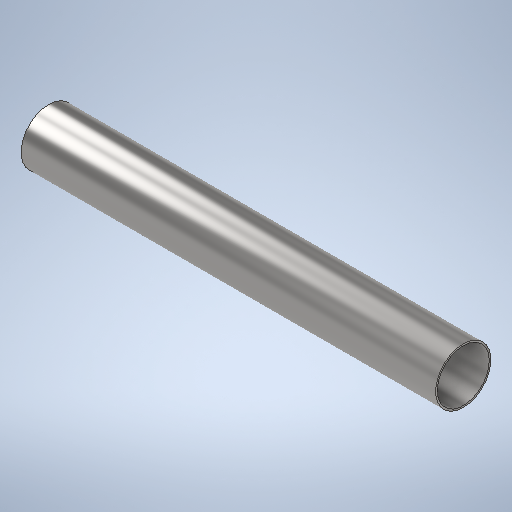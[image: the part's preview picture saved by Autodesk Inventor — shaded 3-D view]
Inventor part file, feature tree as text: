
AUTODESK INVENTOR PART (.ipt)
format: ipt  version: 2025.2 (Build 292293000, 293)  size: 261,120 bytes
history: native  units: mm
features: other x1, sketch x1
ambient origin geometry x8: Origin, YZ Plane, XZ Plane, XY Plane, X Axis, Y Axis, Z Axis, Center Point
bodies: Body1 (feature_tree)
feature tree (2):
  other  "Revolução1"
  sketch  "Esboço1"  dims[d0=750.0mm d1=50.0mm d2=3.0mm d5=90.0deg d6=0.872665mm]
